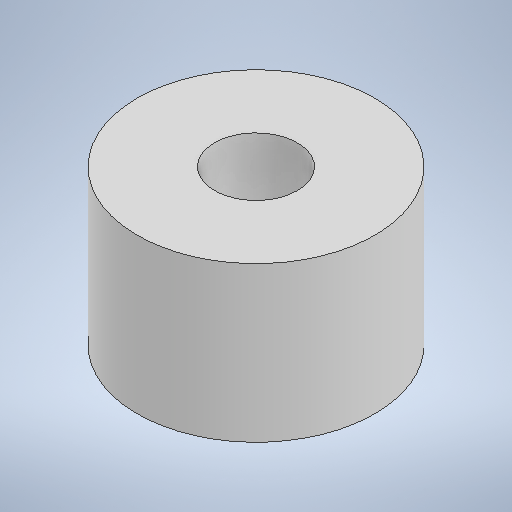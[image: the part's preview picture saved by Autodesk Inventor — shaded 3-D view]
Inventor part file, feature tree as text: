
AUTODESK INVENTOR PART (.ipt)
format: ipt  version: 2025.1 (Build 291241000, 241)  size: 193,024 bytes
history: native  units: in
note: dims shown in document units (in); Inventor stores cm internally (conversion verified against a paired STEP export)
features: extrude x1, sketch x1
ambient origin geometry x8: Origin, YZ Plane, XZ Plane, XY Plane, X Axis, Y Axis, Z Axis, Center Point
bodies: Solid1 (feature_tree)
feature tree (2):
  extrude  "Extrusion1"  Depth=0.25in
  sketch  "Sketch1"  dims[d0=0.125in d1=0.1339in d2=0.25in d3=0.0in]
